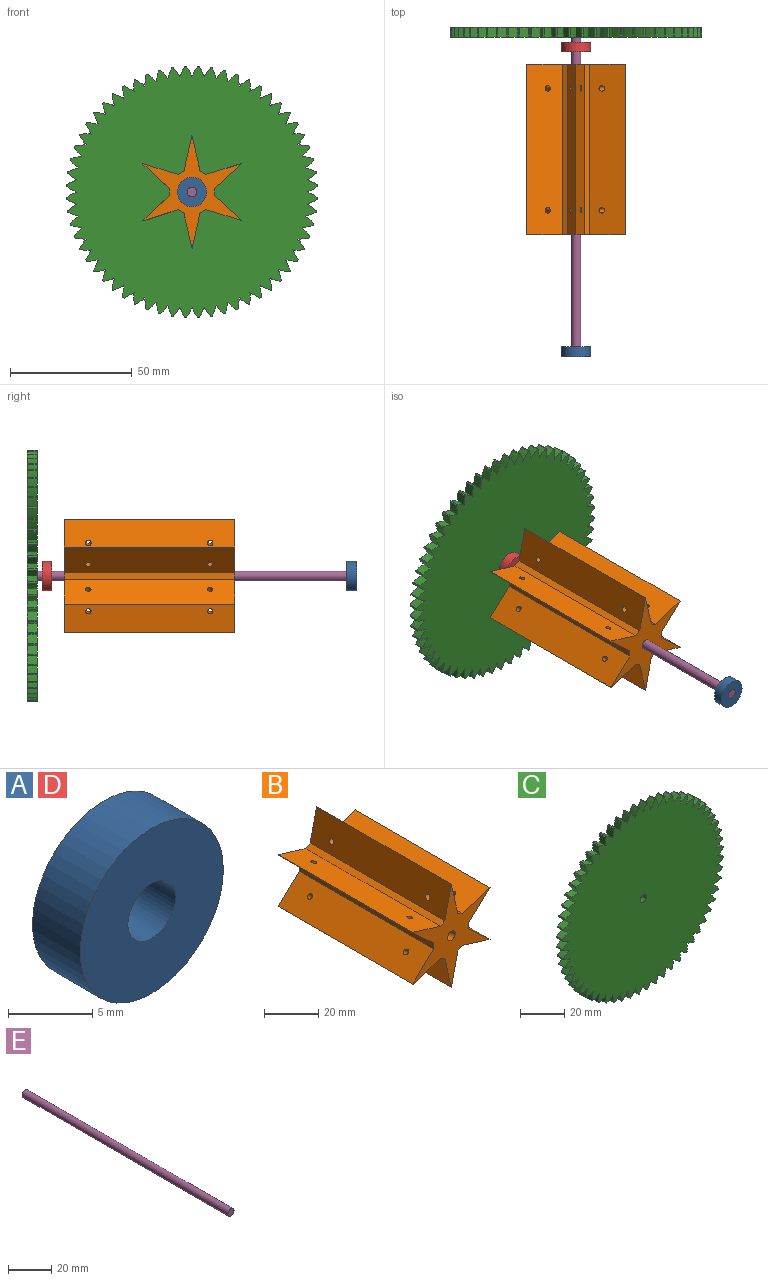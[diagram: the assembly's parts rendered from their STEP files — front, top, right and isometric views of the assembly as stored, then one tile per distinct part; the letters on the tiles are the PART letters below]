
ASSEMBLY  parts=5 mates=4
PART A: 4 faces, bbox 12x4x12 mm
  f0: cylinder r=2mm len=4mm, axis (0,1,0), area 50.3mm2, adj f2,f3
  f1: cylinder r=6mm len=12mm, axis (0,1,0), area 150.8mm2, adj f2,f3
  f2: plane 12x12mm, normal (0,-1,0), area 100.5mm2, adj f0,f1
  f3: plane 12x12mm, normal (0,1,0), area 100.5mm2, adj f0,f1
PART B: 35 faces, bbox 40.5x70.2x46.7 mm
  f0: plane 70x14.73mm, normal (0.98,0,0.22), area 1049.7mm2, adj f1,f15,f16,f27,f28,f32
  f1: plane 70.22x14.95mm, normal (-0.98,0,0.22), area 1048.8mm2, adj f0,f15,f16,f27,f28,f31
  f2: plane 70x11.08mm, normal (0.68,0,-0.73), area 1049.7mm2, adj f3,f15,f16,f25,f26,f33
  f3: plane 70.22x14.65mm, normal (-0.3,0,0.96), area 1048.8mm2, adj f2,f15,f16,f25,f26,f32
  f4: plane 70x14.43mm, normal (-0.3,0,-0.96), area 1049.7mm2, adj f5,f15,f16,f23,f24,f34
  f5: plane 70.22x11.3mm, normal (0.68,0,0.73), area 1048.8mm2, adj f4,f15,f16,f23,f24,f33
  f6: plane 70x14.69mm, normal (-0.98,0,-0.22), area 1046.9mm2, adj f7,f15,f16,f21,f22,f29
  f7: plane 70.22x14.95mm, normal (0.98,0,-0.22), area 1048.8mm2, adj f6,f15,f16,f21,f22,f34
  f8: plane 70x11.07mm, normal (-0.68,0,0.73), area 1048.4mm2, adj f13,f15,f16,f19,f20,f30
  f9: plane 70.21x14.23mm, normal (0.31,0,-0.95), area 1025mm2, adj f13,f15,f16,f19,f20,f29
  f10: plane 70.22x11.27mm, normal (-0.67,0,-0.74), area 1038.1mm2, adj f12,f15,f16,f17,f18,f30
  f11: plane 70x14.43mm, normal (0.3,0,0.96), area 1049.7mm2, adj f12,f15,f16,f17,f18,f31
  f12: plane 70x0.2mm, normal (-1,0,0), area 14.1mm2, adj f10,f11,f15,f16
  f13: plane 70x0.39mm, normal (-0.5,0,-0.87), area 31.4mm2, adj f8,f9,f15,f16
  f14: cylinder r=2mm len=70mm, axis (0,1,0), area 879.6mm2, adj f15,f16
  f15: plane 46.5x40.27mm, normal (0,-1,0), area 532.7mm2, adj f0,f1,f2,f3,f4,f5,f6,f7
  f16: plane 46.5x40.27mm, normal (0,1,0), area 532.7mm2, adj f0,f1,f2,f3,f4,f5,f6,f7
  f17: cylinder r=1.1mm len=5.33mm, axis (0.3,0,0.96), area 30.3mm2, adj f10,f11
  f18: cylinder r=1.1mm len=5.33mm, axis (0.3,0,0.96), area 30.3mm2, adj f10,f11
  f19: cylinder r=1.1mm len=5.14mm, axis (-0.68,0,0.73), area 30.9mm2, adj f8,f9
  f20: cylinder r=1.1mm len=5.14mm, axis (-0.68,0,0.73), area 30.9mm2, adj f8,f9
  f21: cylinder r=1.1mm len=5.21mm, axis (-0.98,0,-0.22), area 29.8mm2, adj f6,f7
  f22: cylinder r=1.1mm len=5.21mm, axis (-0.98,0,-0.22), area 29.8mm2, adj f6,f7
  f23: cylinder r=1.1mm len=5.28mm, axis (-0.3,0,-0.96), area 29.8mm2, adj f4,f5
  f24: cylinder r=1.1mm len=5.28mm, axis (-0.3,0,-0.96), area 29.8mm2, adj f4,f5
  f25: cylinder r=1.1mm len=5.05mm, axis (0.68,0,-0.73), area 29.8mm2, adj f2,f3
  f26: cylinder r=1.1mm len=5.05mm, axis (0.68,0,-0.73), area 29.8mm2, adj f2,f3
  f27: cylinder r=1.1mm len=5.21mm, axis (0.98,0,0.22), area 29.8mm2, adj f0,f1
  f28: cylinder r=1.1mm len=5.21mm, axis (0.98,0,0.22), area 29.8mm2, adj f0,f1
  f29: plane 70x2.39mm, normal (-0.49,0,-0.87), area 192mm2, adj f6,f9,f15,f16
  f30: plane 70x2.73mm, normal (-1,0,0), area 191.1mm2, adj f8,f10,f15,f16
  f31: plane 70x2.35mm, normal (-0.5,0,0.87), area 190.3mm2, adj f1,f11,f15,f16
  f32: plane 70x2.35mm, normal (0.5,0,0.87), area 190.3mm2, adj f0,f3,f15,f16
  f33: plane 70x2.72mm, normal (1,0,0), area 190.3mm2, adj f2,f5,f15,f16
  f34: plane 70x2.35mm, normal (0.5,0,-0.87), area 190.3mm2, adj f4,f7,f15,f16
PART C: 183 faces, bbox 103.2x4x103.2 mm
  f0: extruded ~4.11x4mm, area 19mm2, adj f1,f179,f181,f182
  f1: extruded ~4.73x4mm, area 19mm2, adj f0,f2,f181,f182
  f2: cylinder r=51.67mm len=4mm, axis (0,1,0), area 2.5mm2, adj f1,f3,f181,f182
  f3: extruded ~4x3.85mm, area 19mm2, adj f2,f4,f181,f182
  f4: extruded ~4.7x4mm, area 19mm2, adj f3,f5,f181,f182
  f5: cylinder r=51.67mm len=4mm, axis (0,1,0), area 2.5mm2, adj f4,f6,f181,f182
  f6: extruded ~4x3.54mm, area 19mm2, adj f5,f7,f181,f182
  f7: extruded ~4.62x4mm, area 19mm2, adj f6,f8,f181,f182
  f8: cylinder r=51.67mm len=4mm, axis (0,1,0), area 2.5mm2, adj f7,f9,f181,f182
  f9: extruded ~4x3.5mm, area 19mm2, adj f8,f10,f181,f182
  f10: extruded ~4.49x4mm, area 19mm2, adj f9,f11,f181,f182
  f11: cylinder r=51.67mm len=4mm, axis (0,1,0), area 2.5mm2, adj f10,f12,f181,f182
  f12: extruded ~4x3.81mm, area 19mm2, adj f11,f13,f181,f182
  f13: extruded ~4.31x4mm, area 19mm2, adj f12,f14,f181,f182
  f14: cylinder r=51.67mm len=4mm, axis (0,1,0), area 2.5mm2, adj f13,f15,f181,f182
  f15: extruded ~4.08x4mm, area 19mm2, adj f14,f16,f181,f182
  f16: extruded ~4.08x4mm, area 19mm2, adj f15,f17,f181,f182
  f17: cylinder r=51.67mm len=4mm, axis (0,1,0), area 2.5mm2, adj f16,f18,f181,f182
  f18: extruded ~4.31x4mm, area 19mm2, adj f17,f19,f181,f182
  f19: extruded ~4x3.81mm, area 19mm2, adj f18,f20,f181,f182
  f20: cylinder r=51.67mm len=4mm, axis (0,1,0), area 2.5mm2, adj f19,f21,f181,f182
  f21: extruded ~4.49x4mm, area 19mm2, adj f20,f22,f181,f182
  f22: extruded ~4x3.5mm, area 19mm2, adj f21,f23,f181,f182
  f23: cylinder r=51.67mm len=4mm, axis (0,1,0), area 2.5mm2, adj f22,f24,f181,f182
  f24: extruded ~4.62x4mm, area 19mm2, adj f23,f25,f181,f182
  f25: extruded ~4x3.54mm, area 19mm2, adj f24,f26,f181,f182
  f26: cylinder r=51.67mm len=4mm, axis (0,1,0), area 2.5mm2, adj f25,f27,f181,f182
  f27: extruded ~4.7x4mm, area 19mm2, adj f26,f28,f181,f182
  f28: extruded ~4x3.85mm, area 19mm2, adj f27,f29,f181,f182
  f29: cylinder r=51.67mm len=4mm, axis (0,1,0), area 2.5mm2, adj f28,f30,f181,f182
  f30: extruded ~4.73x4mm, area 19mm2, adj f29,f31,f181,f182
  f31: extruded ~4.11x4mm, area 19mm2, adj f30,f32,f181,f182
  f32: cylinder r=51.67mm len=4mm, axis (0,1,0), area 2.5mm2, adj f31,f33,f181,f182
  f33: extruded ~4.71x4mm, area 19mm2, adj f32,f34,f181,f182
  f34: extruded ~4.34x4mm, area 19mm2, adj f33,f35,f181,f182
  f35: cylinder r=51.67mm len=4mm, axis (0,1,0), area 2.5mm2, adj f34,f36,f181,f182
  f36: extruded ~4.64x4mm, area 19mm2, adj f35,f37,f181,f182
  f37: extruded ~4.51x4mm, area 19mm2, adj f36,f38,f181,f182
  f38: cylinder r=51.67mm len=4mm, axis (0,1,0), area 2.5mm2, adj f37,f39,f181,f182
  f39: extruded ~4.51x4mm, area 19mm2, adj f38,f40,f181,f182
  f40: extruded ~4.64x4mm, area 19mm2, adj f39,f41,f181,f182
  f41: cylinder r=51.67mm len=4mm, axis (0,1,0), area 2.5mm2, adj f40,f42,f181,f182
  f42: extruded ~4.34x4mm, area 19mm2, adj f41,f43,f181,f182
  f43: extruded ~4.71x4mm, area 19mm2, adj f42,f44,f181,f182
  f44: cylinder r=51.67mm len=4mm, axis (0,1,0), area 2.5mm2, adj f43,f45,f181,f182
  f45: extruded ~4.11x4mm, area 19mm2, adj f44,f46,f181,f182
  f46: extruded ~4.73x4mm, area 19mm2, adj f45,f47,f181,f182
  f47: cylinder r=51.67mm len=4mm, axis (0,1,0), area 2.5mm2, adj f46,f48,f181,f182
  f48: extruded ~4x3.85mm, area 19mm2, adj f47,f49,f181,f182
  f49: extruded ~4.7x4mm, area 19mm2, adj f48,f50,f181,f182
  f50: cylinder r=51.67mm len=4mm, axis (0,1,0), area 2.5mm2, adj f49,f51,f181,f182
  f51: extruded ~4x3.54mm, area 19mm2, adj f50,f52,f181,f182
  f52: extruded ~4.62x4mm, area 19mm2, adj f51,f53,f181,f182
  f53: cylinder r=51.67mm len=4mm, axis (0,1,0), area 2.5mm2, adj f52,f54,f181,f182
  f54: extruded ~4x3.5mm, area 19mm2, adj f53,f55,f181,f182
  f55: extruded ~4.49x4mm, area 19mm2, adj f54,f56,f181,f182
  f56: cylinder r=51.67mm len=4mm, axis (0,1,0), area 2.5mm2, adj f55,f57,f181,f182
  f57: extruded ~4x3.81mm, area 19mm2, adj f56,f58,f181,f182
  f58: extruded ~4.31x4mm, area 19mm2, adj f57,f59,f181,f182
  f59: cylinder r=51.67mm len=4mm, axis (0,1,0), area 2.5mm2, adj f58,f60,f181,f182
  f60: extruded ~4.08x4mm, area 19mm2, adj f59,f61,f181,f182
  f61: extruded ~4.08x4mm, area 19mm2, adj f60,f62,f181,f182
  f62: cylinder r=51.67mm len=4mm, axis (0,1,0), area 2.5mm2, adj f61,f63,f181,f182
  f63: extruded ~4.31x4mm, area 19mm2, adj f62,f64,f181,f182
  f64: extruded ~4x3.81mm, area 19mm2, adj f63,f65,f181,f182
  f65: cylinder r=51.67mm len=4mm, axis (0,1,0), area 2.5mm2, adj f64,f66,f181,f182
  f66: extruded ~4.49x4mm, area 19mm2, adj f65,f67,f181,f182
  f67: extruded ~4x3.5mm, area 19mm2, adj f66,f68,f181,f182
  f68: cylinder r=51.67mm len=4mm, axis (0,1,0), area 2.5mm2, adj f67,f69,f181,f182
  f69: extruded ~4.62x4mm, area 19mm2, adj f68,f70,f181,f182
  f70: extruded ~4x3.54mm, area 19mm2, adj f69,f71,f181,f182
  f71: cylinder r=51.67mm len=4mm, axis (0,1,0), area 2.5mm2, adj f70,f72,f181,f182
  f72: extruded ~4.7x4mm, area 19mm2, adj f71,f73,f181,f182
  f73: extruded ~4x3.85mm, area 19mm2, adj f72,f74,f181,f182
  f74: cylinder r=51.67mm len=4mm, axis (0,1,0), area 2.5mm2, adj f73,f75,f181,f182
  f75: extruded ~4.73x4mm, area 19mm2, adj f74,f76,f181,f182
  f76: extruded ~4.11x4mm, area 19mm2, adj f75,f77,f181,f182
  f77: cylinder r=51.67mm len=4mm, axis (0,1,0), area 2.5mm2, adj f76,f78,f181,f182
  f78: extruded ~4.71x4mm, area 19mm2, adj f77,f79,f181,f182
  f79: extruded ~4.34x4mm, area 19mm2, adj f78,f80,f181,f182
  f80: cylinder r=51.67mm len=4mm, axis (0,1,0), area 2.5mm2, adj f79,f81,f181,f182
  f81: extruded ~4.64x4mm, area 19mm2, adj f80,f82,f181,f182
  f82: extruded ~4.51x4mm, area 19mm2, adj f81,f83,f181,f182
  f83: cylinder r=51.67mm len=4mm, axis (0,1,0), area 2.5mm2, adj f82,f84,f181,f182
  f84: extruded ~4.51x4mm, area 19mm2, adj f83,f85,f181,f182
  f85: extruded ~4.64x4mm, area 19mm2, adj f84,f86,f181,f182
  f86: cylinder r=51.67mm len=4mm, axis (0,1,0), area 2.5mm2, adj f85,f87,f181,f182
  f87: extruded ~4.34x4mm, area 19mm2, adj f86,f88,f181,f182
  f88: extruded ~4.71x4mm, area 19mm2, adj f87,f89,f181,f182
  f89: cylinder r=51.67mm len=4mm, axis (0,1,0), area 2.5mm2, adj f88,f90,f181,f182
  f90: extruded ~4.11x4mm, area 19mm2, adj f89,f91,f181,f182
  f91: extruded ~4.73x4mm, area 19mm2, adj f90,f92,f181,f182
  f92: cylinder r=51.67mm len=4mm, axis (0,1,0), area 2.5mm2, adj f91,f93,f181,f182
  f93: extruded ~4x3.85mm, area 19mm2, adj f92,f94,f181,f182
  f94: extruded ~4.7x4mm, area 19mm2, adj f93,f95,f181,f182
  f95: cylinder r=51.67mm len=4mm, axis (0,1,0), area 2.5mm2, adj f94,f96,f181,f182
  f96: extruded ~4x3.54mm, area 19mm2, adj f95,f97,f181,f182
  f97: extruded ~4.62x4mm, area 19mm2, adj f96,f98,f181,f182
  f98: cylinder r=51.67mm len=4mm, axis (0,1,0), area 2.5mm2, adj f97,f99,f181,f182
  f99: extruded ~4x3.5mm, area 19mm2, adj f98,f100,f181,f182
  f100: extruded ~4.49x4mm, area 19mm2, adj f99,f101,f181,f182
  f101: cylinder r=51.67mm len=4mm, axis (0,1,0), area 2.5mm2, adj f100,f102,f181,f182
  f102: extruded ~4x3.81mm, area 19mm2, adj f101,f103,f181,f182
  f103: extruded ~4.31x4mm, area 19mm2, adj f102,f104,f181,f182
  f104: cylinder r=51.67mm len=4mm, axis (0,1,0), area 2.5mm2, adj f103,f105,f181,f182
  f105: extruded ~4.08x4mm, area 19mm2, adj f104,f106,f181,f182
  f106: extruded ~4.08x4mm, area 19mm2, adj f105,f107,f181,f182
  f107: cylinder r=51.67mm len=4mm, axis (0,1,0), area 2.5mm2, adj f106,f108,f181,f182
  f108: extruded ~4.31x4mm, area 19mm2, adj f107,f109,f181,f182
  f109: extruded ~4x3.81mm, area 19mm2, adj f108,f110,f181,f182
  f110: cylinder r=51.67mm len=4mm, axis (0,1,0), area 2.5mm2, adj f109,f111,f181,f182
  f111: extruded ~4.49x4mm, area 19mm2, adj f110,f112,f181,f182
  f112: extruded ~4x3.5mm, area 19mm2, adj f111,f113,f181,f182
  f113: cylinder r=51.67mm len=4mm, axis (0,1,0), area 2.5mm2, adj f112,f114,f181,f182
  f114: extruded ~4.62x4mm, area 19mm2, adj f113,f115,f181,f182
  f115: extruded ~4x3.54mm, area 19mm2, adj f114,f116,f181,f182
  f116: cylinder r=51.67mm len=4mm, axis (0,1,0), area 2.5mm2, adj f115,f117,f181,f182
  f117: extruded ~4.7x4mm, area 19mm2, adj f116,f118,f181,f182
  f118: extruded ~4x3.85mm, area 19mm2, adj f117,f119,f181,f182
  f119: cylinder r=51.67mm len=4mm, axis (0,1,0), area 2.5mm2, adj f118,f120,f181,f182
  f120: extruded ~4.73x4mm, area 19mm2, adj f119,f121,f181,f182
  f121: extruded ~4.11x4mm, area 19mm2, adj f120,f122,f181,f182
  f122: cylinder r=51.67mm len=4mm, axis (0,1,0), area 2.5mm2, adj f121,f123,f181,f182
  f123: extruded ~4.71x4mm, area 19mm2, adj f122,f124,f181,f182
  f124: extruded ~4.34x4mm, area 19mm2, adj f123,f125,f181,f182
  f125: cylinder r=51.67mm len=4mm, axis (0,1,0), area 2.5mm2, adj f124,f126,f181,f182
  f126: extruded ~4.64x4mm, area 19mm2, adj f125,f127,f181,f182
  f127: extruded ~4.51x4mm, area 19mm2, adj f126,f128,f181,f182
  f128: cylinder r=51.67mm len=4mm, axis (0,1,0), area 2.5mm2, adj f127,f129,f181,f182
  f129: extruded ~4.51x4mm, area 19mm2, adj f128,f130,f181,f182
  f130: extruded ~4.64x4mm, area 19mm2, adj f129,f131,f181,f182
  f131: cylinder r=51.67mm len=4mm, axis (0,1,0), area 2.5mm2, adj f130,f132,f181,f182
  f132: extruded ~4.34x4mm, area 19mm2, adj f131,f133,f181,f182
  f133: extruded ~4.71x4mm, area 19mm2, adj f132,f134,f181,f182
  f134: cylinder r=51.67mm len=4mm, axis (0,1,0), area 2.5mm2, adj f133,f135,f181,f182
  f135: extruded ~4.11x4mm, area 19mm2, adj f134,f136,f181,f182
  f136: extruded ~4.73x4mm, area 19mm2, adj f135,f137,f181,f182
  f137: cylinder r=51.67mm len=4mm, axis (0,1,0), area 2.5mm2, adj f136,f138,f181,f182
  f138: extruded ~4x3.85mm, area 19mm2, adj f137,f139,f181,f182
  f139: extruded ~4.7x4mm, area 19mm2, adj f138,f140,f181,f182
  f140: cylinder r=51.67mm len=4mm, axis (0,1,0), area 2.5mm2, adj f139,f141,f181,f182
  f141: extruded ~4x3.54mm, area 19mm2, adj f140,f142,f181,f182
  f142: extruded ~4.62x4mm, area 19mm2, adj f141,f143,f181,f182
  f143: cylinder r=51.67mm len=4mm, axis (0,1,0), area 2.5mm2, adj f142,f144,f181,f182
  f144: extruded ~4x3.5mm, area 19mm2, adj f143,f145,f181,f182
  f145: extruded ~4.49x4mm, area 19mm2, adj f144,f146,f181,f182
  f146: cylinder r=51.67mm len=4mm, axis (0,1,0), area 2.5mm2, adj f145,f147,f181,f182
  f147: extruded ~4x3.81mm, area 19mm2, adj f146,f148,f181,f182
  f148: extruded ~4.31x4mm, area 19mm2, adj f147,f149,f181,f182
  f149: cylinder r=51.67mm len=4mm, axis (0,1,0), area 2.5mm2, adj f148,f150,f181,f182
  f150: extruded ~4.08x4mm, area 19mm2, adj f149,f151,f181,f182
  f151: extruded ~4.08x4mm, area 19mm2, adj f150,f152,f181,f182
  f152: cylinder r=51.67mm len=4mm, axis (0,1,0), area 2.5mm2, adj f151,f153,f181,f182
  f153: extruded ~4.31x4mm, area 19mm2, adj f152,f154,f181,f182
  f154: extruded ~4x3.81mm, area 19mm2, adj f153,f155,f181,f182
  f155: cylinder r=51.67mm len=4mm, axis (0,1,0), area 2.5mm2, adj f154,f156,f181,f182
  f156: extruded ~4.49x4mm, area 19mm2, adj f155,f157,f181,f182
  f157: extruded ~4x3.5mm, area 19mm2, adj f156,f158,f181,f182
  f158: cylinder r=51.67mm len=4mm, axis (0,1,0), area 2.5mm2, adj f157,f159,f181,f182
  f159: extruded ~4.62x4mm, area 19mm2, adj f158,f160,f181,f182
  f160: extruded ~4x3.54mm, area 19mm2, adj f159,f161,f181,f182
  f161: cylinder r=51.67mm len=4mm, axis (0,1,0), area 2.5mm2, adj f160,f162,f181,f182
  f162: extruded ~4.7x4mm, area 19mm2, adj f161,f163,f181,f182
  f163: extruded ~4x3.85mm, area 19mm2, adj f162,f164,f181,f182
  f164: cylinder r=51.67mm len=4mm, axis (0,1,0), area 2.5mm2, adj f163,f165,f181,f182
  f165: extruded ~4.73x4mm, area 19mm2, adj f164,f166,f181,f182
  f166: extruded ~4.11x4mm, area 19mm2, adj f165,f167,f181,f182
  f167: cylinder r=51.67mm len=4mm, axis (0,1,0), area 2.5mm2, adj f166,f168,f181,f182
  f168: extruded ~4.71x4mm, area 19mm2, adj f167,f169,f181,f182
  f169: extruded ~4.34x4mm, area 19mm2, adj f168,f170,f181,f182
  f170: cylinder r=51.67mm len=4mm, axis (0,1,0), area 2.5mm2, adj f169,f171,f181,f182
  f171: extruded ~4.64x4mm, area 19mm2, adj f170,f172,f181,f182
  f172: extruded ~4.51x4mm, area 19mm2, adj f171,f173,f181,f182
  f173: cylinder r=51.67mm len=4mm, axis (0,1,0), area 2.5mm2, adj f172,f174,f181,f182
  f174: extruded ~4.51x4mm, area 19mm2, adj f173,f175,f181,f182
  f175: extruded ~4.64x4mm, area 19mm2, adj f174,f176,f181,f182
  f176: cylinder r=51.67mm len=4mm, axis (0,1,0), area 2.5mm2, adj f175,f177,f181,f182
  f177: extruded ~4.34x4mm, area 19mm2, adj f176,f178,f181,f182
  f178: extruded ~4.71x4mm, area 19mm2, adj f177,f179,f181,f182
  f179: cylinder r=51.67mm len=4mm, axis (0,1,0), area 2.5mm2, adj f0,f178,f181,f182
  f180: cylinder r=2mm len=4mm, axis (0,1,0), area 50.3mm2, adj f181,f182
  f181: plane 103.23x103.23mm, normal (0,-1,0), area 7821.2mm2, adj f0,f1,f2,f3,f4,f5,f6,f7
  f182: plane 103.23x103.23mm, normal (0,1,0), area 7821.2mm2, adj f0,f1,f2,f3,f4,f5,f6,f7
PART D: same geometry as A
PART E: 3 faces, bbox 4x135x4 mm
  f0: cylinder r=2mm len=135mm, axis (0,1,0), area 1696.5mm2, adj f1,f2
  f1: plane 4x4mm, normal (0,-1,0), area 12.6mm2, adj f0
  f2: plane 4x4mm, normal (0,1,0), area 12.6mm2, adj f0
PLACE A t=(-41.48,-78.98,-33.99)mm
PLACE B t=(-41.48,37.02,-33.99)mm
PLACE C t=(-41.48,52.02,-33.99)mm
PLACE D t=(-41.48,46.02,-33.99)mm
PLACE E t=(-41.48,27.02,-33.99)mm
MATE fastened A.f0 <-> E.f0  axis (0,-1,0) through (-41.48,-82.98,-33.99)mm
MATE fastened B.f14 <-> E.f0  axis (0,1,0) through (-41.48,37.02,-33.99)mm
MATE revolute D.f0 <-> E.f0  axis (0,1,0) through (-41.48,46.02,-33.99)mm
MATE fastened E.f0 <-> C.f2  axis (0,1,0) through (-41.48,52.02,-33.99)mm
